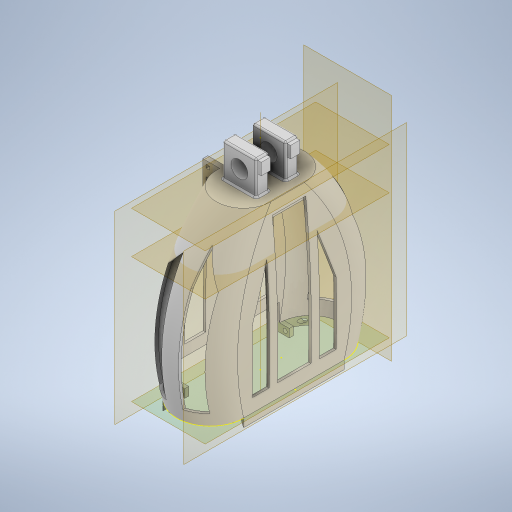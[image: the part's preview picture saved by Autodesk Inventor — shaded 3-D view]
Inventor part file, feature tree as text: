
AUTODESK INVENTOR PART (.ipt)
format: ipt  version: 2023 (Build 270158000, 158)  size: 1,000,448 bytes
history: native  units: mm
features: sketch x35, extrude x16, plane x6, fillet x3, chamfer x2, mirror x2, loft x1, shell x1, projected_geometry x1
ambient origin geometry x8: Origin, YZ Plane, XZ Plane, XY Plane, X Axis, Y Axis, Z Axis, Center Point
bodies: Solid1 (feature_tree)
feature tree (67):
  sketch  "Sketch1"  dims[d0=120.0mm d1=80.0mm d2=20.0mm]
  plane  "Work Plane1"
  sketch  "Sketch2"  dims[d3=200.0mm d4=40.0mm]
  plane  "Work Plane2"
  sketch  "Sketch3"  dims[d5=65.0mm d6=150.0mm]
  plane  "Work Plane3"
  loft  "Loft1"
  shell  "Shell1"  Thickness=20.0mm
  sketch  "Sketch4"  dims[d7=100.0mm d8=75.0mm]
  plane  "Work Plane4"
  extrude  "Extrusion1"  Depth=40.0mm
  sketch  "Sketch10"  dims[d15=3.0mm]
  extrude  "Extrusion2"  Depth=150.0mm
  sketch  "Sketch12"  dims[d22=40.0mm]
  extrude  "Extrusion3"  Depth=75.0mm
  extrude  "Extrusion4"  TaperAngle=0.0deg  [1 undecoded]
  fillet  "Fillet1"  [1 undecoded]
  chamfer  "Chamfer1"  Distance=10.0mm
  chamfer  "Chamfer2"  Distance=40.0mm
  extrude  "Extrusion5"  Depth=50.0mm TaperAngle=0.0deg
  extrude  "Extrusion7"  Depth=40.0mm TaperAngle=0.0deg
  mirror  "Mirror2"
  mirror  "Mirror3"
  sketch  "Sketch18"  dims[d36=2.0mm d37=2.0mm d38=45.0deg d39=55.0mm]
  sketch  "Sketch19"  dims[d40=25.0mm d41=12.5mm]
  extrude  "Extrusion8"  Depth=2.0mm TaperAngle=45.0deg
  fillet  "Fillet2"  Radius=55.0mm
  sketch  "Sketch21"  dims[d44=2.0mm d45=2.0mm]
  sketch  "Sketch22"  dims[d46=10.0mm d47=0.0mm d55=4.0mm]
  sketch  "Sketch23"  dims[d56=5.0mm d57=5.0mm d58=50.0mm d59=0.0mm]
  sketch  "Sketch24"  dims[d60=3.0mm d61=10.0mm d62=0.0mm]
  sketch  "Sketch25"  dims[d63=20.0mm d64=50.0mm]
  sketch  "Sketch26"  dims[d65=129.0mm d66=50.0mm]
  sketch  "Sketch27"  dims[d67=6.0mm d68=6.0mm]
  sketch  "Sketch28"  dims[d69=10.0mm d70=0.0mm]
  extrude  "Extrusion9"  Depth=12.5mm
  extrude  "Extrusion10"  Depth=5.0mm
  extrude  "Extrusion11"  Depth=2.0mm
  extrude  "Extrusion12"  Depth=4.0mm
  extrude  "Extrusion13"  Depth=5.0mm
  fillet  "Fillet3"  Radius=50.0mm
  extrude  "Extrusion14"  Depth=10.0mm TaperAngle=0.0deg
  sketch  "Sketch34"  dims[d78=4.0mm]
  sketch  "Sketch35"  dims[d79=4.0mm]
  sketch  "Sketch36"  dims[d80=4.0mm]
  plane  "Work Plane5"
  sketch  "Sketch37"  dims[d81=9.0mm]
  extrude  "Extrusion15"  Depth=50.0mm
  extrude  "Extrusion16"  Depth=50.0mm
  plane  "Work Plane6"
  extrude  "Extrusion17"  Depth=6.0mm
  sketch  "Sketch9"  dims[d9=0.0mm d10=90.0deg d11=0.0mm d12=90.0deg d13=0.0mm d14=90.0deg]
  projected_geometry  "Projected Loop1"
  sketch  "Sketch11"  dims[d19=21.0mm d20=10.0mm d21=0.0mm]
  sketch  "Sketch13"  dims[d23=50.0mm d24=40.0mm d25=0.0mm]
  sketch  "Sketch14"  dims[d26=20.0mm d27=50.0mm d28=0.0mm]
  sketch  "Sketch15"  dims[d29=20.0mm d30=40.0mm d31=0.0mm]
  sketch  "Sketch17"  dims[d32=2.0mm d33=2.0mm d34=2.0mm d35=45.0deg]
  sketch  "Sketch20"  dims[d42=5.0mm d43=5.0mm]
  sketch  "Sketch29"  dims[d71=6.0mm]
  sketch  "Sketch30"  dims[d72=6.0mm]
  sketch  "Sketch31"  dims[d73=9.0mm d74=0.0mm]
  sketch  "Sketch32"  dims[d75=12.0mm d76=0.0mm]
  sketch  "Sketch33"  dims[d77=12.0mm]
  sketch  "Sketch38"  dims[d82=4.0mm]
  sketch  "Sketch39"  dims[d83=9.0mm]
  sketch  "Sketch40"  dims[d84=4.0mm d85=9.0mm d86=4.0mm d87=40.0mm d88=0.0mm d89=11.0mm d90=4.0mm d91=4.0mm d92=0.0mm d93=2.0mm d94=10.0mm d95=0.0mm d96=82.5mm d97=170.0mm d98=40.0mm d99=75.0mm d100=20.0mm d101=75.0mm d102=20.0mm d103=60.0mm d104=60.0mm d105=10.0mm d106=0.0mm d107=40.0mm d108=25.0mm d109=40.0mm d110=25.0mm d111=75.0mm d112=20.0mm d113=20.0mm d114=25.0mm d115=10.0mm d116=0.0mm d117=-109.5mm d118=20.0mm d119=120.0mm d120=20.0mm d121=30.0mm d122=40.0mm d123=300.0mm d124=0.0mm]
note: 2 required parameter values undecoded (feature->parameter linkage not recoverable at this tier; creation-order binding heuristic only, values carry confidence <= 0.55)
